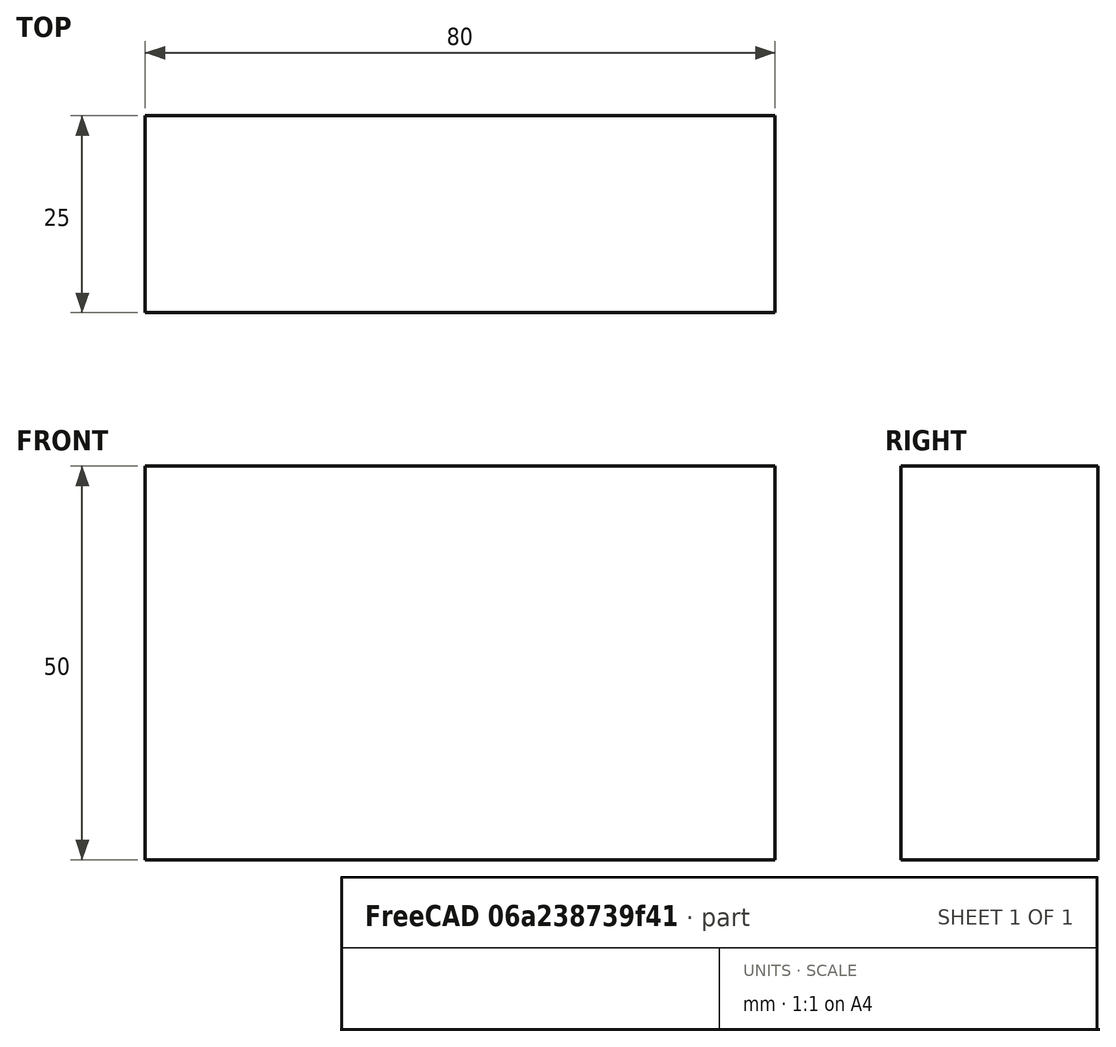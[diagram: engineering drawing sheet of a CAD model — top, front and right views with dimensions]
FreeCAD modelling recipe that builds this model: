
FCSTD DOCUMENT  (FreeCAD 0.15R4671 (Git))
Label: Flat Bar 80x25 EN10058 S235JR
License: All rights reserved
LicenseURL: http://en.wikipedia.org/wiki/All_rights_reserved
objects: Sketcher::SketchObject×1, Part::Extrusion×1
note: 2 computed .brp shape members not serialized (recipe doc carries the construction recipe); baked Part::Feature solids carry a one-line shape summary decoded from their .brp

FEATURE [Sketcher::SketchObject] Sketch
  sketch-geometry (4):
    g0: LineSegment StartX=-40 StartY=-12.5 StartZ=0 EndX=40 EndY=-12.5 EndZ=0
    g1: LineSegment StartX=40 StartY=-12.5 StartZ=0 EndX=40 EndY=12.5 EndZ=0
    g2: LineSegment StartX=40 StartY=12.5 StartZ=0 EndX=-40 EndY=12.5 EndZ=0
    g3: LineSegment StartX=-40 StartY=12.5 StartZ=0 EndX=-40 EndY=-12.5 EndZ=0
  constraints (12):
    c: Coincident(g0,g1)
    c: Coincident(g1,g2)
    c: Coincident(g2,g3)
    c: Coincident(g3,g0)
    c: Horizontal(g0)
    c: Horizontal(g2)
    c: Vertical(g1)
    c: Vertical(g3)
    c: Symmetric(g1,g2,g-2)
    c: Symmetric(g0,g1,g-1)
    c: DistanceY(g1) = 25
    c: DistanceX(g0) = 80
FEATURE [Part::Extrusion] Extrude  label="Flat Bar 80x25 EN10058 S235JR"
  Base = -> Sketch
  Dir = (0,0,50)
  Solid = true
